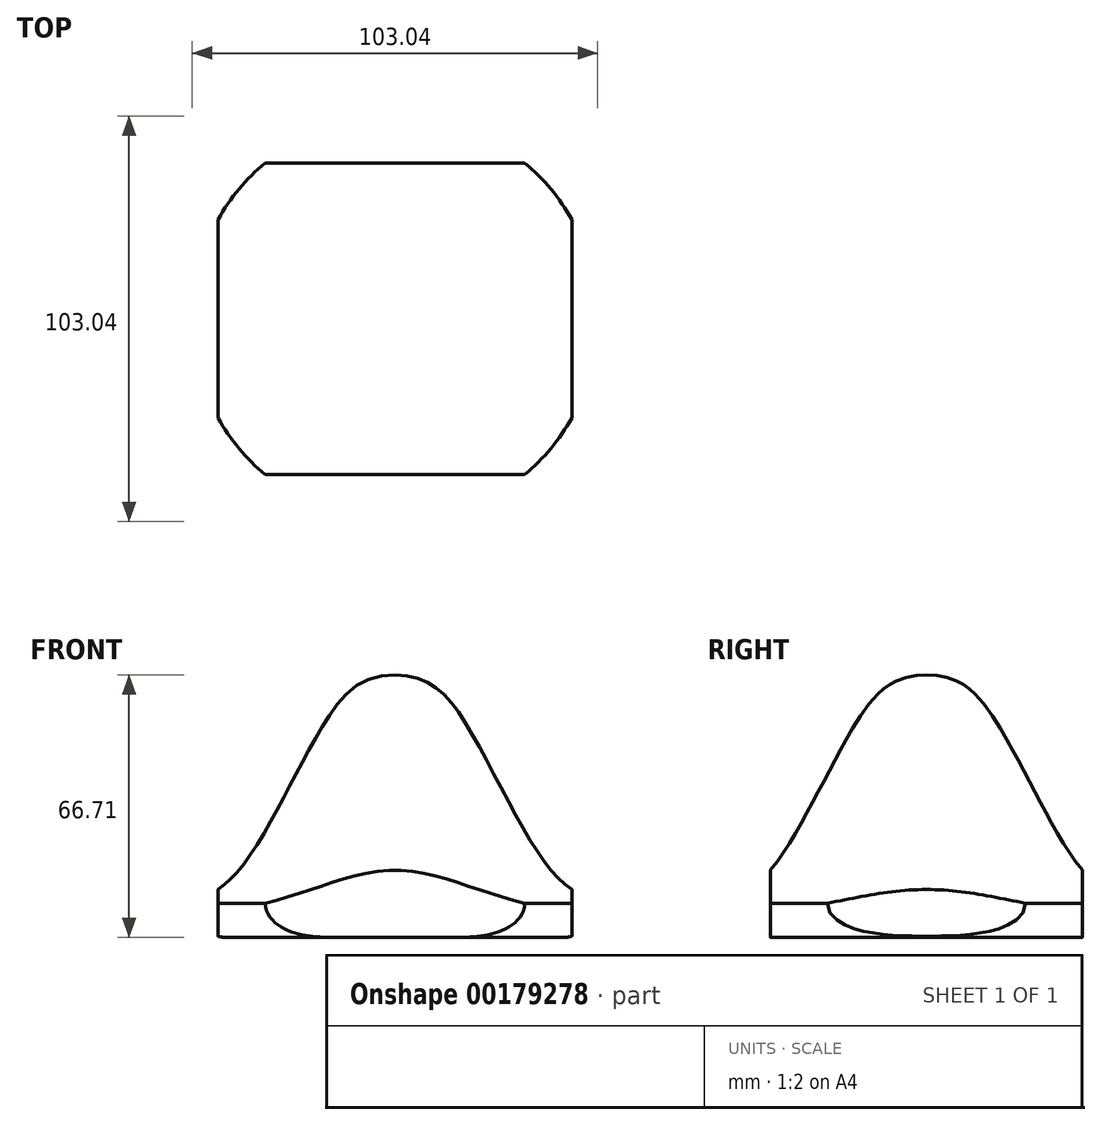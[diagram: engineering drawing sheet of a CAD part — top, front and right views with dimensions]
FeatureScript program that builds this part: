
annotation { "Feature Type Name" : "Feature", "Feature Type Description" : "" }
export const myFeature = defineFeature(function(context is Context, id is Id, definition is map)
    precondition{}
    {
        {
            var Q0;
            Q0=qCreatedBy(makeId("Front.planeOp"),FACE);
            var sketch = newSketch(context, id + "F0", { "sketchPlane" : qUnion([Q0])});
            skFitSpline(sketch, "E0", {"points": [v(0, 66.71) * mm, v(18.2, 54.04) * mm, v(38.54, 18.45) * mm, v(51.52, 8.69) * mm], "startDerivative": vector(87.3, 0) * mm, "endDerivative": vector(57.16, -25) * mm});
            skFitSpline(sketch, "E1", {"points": [v(51.52, 8.69) * mm, v(42.43, 0) * mm], "startDerivative": vector(0, -14.26) * mm, "endDerivative": vector(-15.27, 0) * mm});
            skLineSegment(sketch, "E2", {"start": v(0, 66.71) * mm, "end": v(0, 0) * mm});
            skLineSegment(sketch, "E3", {"start": v(0, 0) * mm, "end": v(42.43, 0) * mm});
            skSolve(sketch);
        }
        {
            var Q0;
            Q0=makeQuery(id+"F0.imprint","IMPRINT",FACE,{"disambiguationData":[TD([[makeQuery(id+"F0.imprint","IMPRINT",EDGE,{"derivedFrom":sQuery(id+"F0.wireOp",EDGE,"E0")}),-1.0]])]});
            var Q1;
            Q1=sQuery(id+"F0.wireOp",EDGE,"E2");
            revolve(context, id + "F1", {"surfaceOperationType" : NewSurfaceOperationType.NEW, "entities" : qUnion([Q0]), "axis" : qUnion([Q1]), "revolveType" : RevolveType.FULL});
        }
        {
            var Q0;
            Q0=qCreatedBy(makeId("Top.planeOp"),FACE);
            var sketch = newSketch(context, id + "F2", { "sketchPlane" : qUnion([Q0])});
            skLineSegment(sketch, "E4.bottom", {"start": v(-44.94, -39.59) * mm, "end": v(44.94, -39.59) * mm});
            skLineSegment(sketch, "E4.top", {"start": v(-44.94, 39.59) * mm, "end": v(44.94, 39.59) * mm});
            skLineSegment(sketch, "E4.left", {"start": v(-44.94, -39.59) * mm, "end": v(-44.94, 39.59) * mm});
            skLineSegment(sketch, "E4.right", {"start": v(44.94, -39.59) * mm, "end": v(44.94, 39.59) * mm});
            skPoint(sketch, "E4.middle", {"position": v(0, 0) * mm});
            skSolve(sketch);
        }
        {
            var Q0;
            Q0 = qSketchRegion(id + "F2", true);
            extrude(context, id + "F3", {"entities" : qUnion([Q0]), "operationType" : NewBodyOperationType.INTERSECT, "endBound" : BoundingType.THROUGH_ALL, "depth" : 25 * mm, "offsetDistance" : 25 * mm});
        }
    });
